# Revit family: GQ Rosenberg 1
name_source: partatom
category: Wyposażenie mechaniczne
revit_build: Autodesk Revit 2017 (Build: 20160225_1515(x64)
units: mm (PartAtom-declared; Revit-internal decimal feet)

## family parameters
Oparty na płaszczyźnie roboczej = Nie
Punkt obliczania pomieszczeń = Nie
Tnij formami wycięć po wczytaniu = Nie
Typ części = Normalny
Współdzielony = Nie
Wymiar okrągłego złącza = Użyj średnicy
Zawsze pionowo = Tak

## types (5) — shared parameters
Częstotliwość = 50 Hz
Data = 09.2018
Klasa szczelnosci silnika (IP) = IP44
Moc = 0 kW
Napięcie = 230 V
Producent = Rosenberg
Prąd = 1 A
Srednica_silnika = 30 mm  [stored 0.0984252 ft]
URL = https://www.rosenberg.pl
Wersja = 1

## per-type parameters (varying)
| type | 200.3BK KS | 250.3BK KS | 300.3BK KS | 350.3DI KS | 400.3DI KS | Ciśnienie | Dlugosc_silnika_przod | Dlugosc_silnika_tyl | Dlugosc_smigla | Grubosc | Grubosc_plyty | Maksymalna dopuszczalna temperatura przetłaczanego medium | Masa | Model | Obroty (1/min) | Promien_wew | Promien_zew | Przepływ poowietrza | Srednica_wew | Srednica_zewnetrzna | Wymiar_obudowy | Wymiar_obudowy/2 |
| 400.3DI KS | Nie | Nie | Nie | Nie | Tak | 65.0 Pa | 41 mm  [stored 0.134514 ft] | 60 mm  [stored 0.19685 ft] | 197 mm  [stored 0.646325 ft] | 88 mm  [stored 0.288714 ft] | 12 mm  [stored 0.0393701 ft] | 45 °C | 7.50 kg | 400.3DI KS | 1430 | 202 mm | 223 mm | 3029.0 m³/h | 403 mm | 445 mm | 540 mm | 270 mm  [stored 0.885827 ft] |
| 250.3BK KS | Nie | Tak | Nie | Nie | Nie | 132.0 Pa | 8 mm  [stored 0.0262467 ft] | 85 mm  [stored 0.278871 ft] | 122 mm | 49 mm  [stored 0.160761 ft] | 6 mm  [stored 0.019685 ft] | 50 °C | 3.50 kg | 250.3BK KS | 2600 | 127 mm | 136 mm | 1152.0 m³/h | 254 mm | 272 mm | 370 mm | 185 mm  [stored 0.606955 ft] |
| 200.3BK KS | Tak | Nie | Nie | Nie | Nie | 132.0 Pa | 15 mm  [stored 0.0492126 ft] | 61 mm  [stored 0.200131 ft] | 95 mm  [stored 0.31168 ft] | 46 mm  [stored 0.150919 ft] | 6 mm  [stored 0.019685 ft] | 50 °C | 1.90 kg | 250.3BK KS | 3375 | 100 mm  [stored 0.328084 ft] | 108 mm | 1152.0 m³/h | 200 mm  [stored 0.656168 ft] | 215 mm | 312 mm | 156 mm  [stored 0.511811 ft] |
| 300.3BK KS | Nie | Nie | Tak | Nie | Nie | 132.0 Pa | 5 mm  [stored 0.0164042 ft] | 60 mm  [stored 0.19685 ft] | 148 mm  [stored 0.485564 ft] | 71 mm  [stored 0.23294 ft] | 11 mm  [stored 0.0360892 ft] | 50 °C | 4.50 kg | 300.3BK KS | 2600 | 153 mm | 165 mm | 1152.0 m³/h | 305 mm  [stored 1.00066 ft] | 330 mm | 430 mm | 215 mm |
| 350.3DI KS | Nie | Nie | Nie | Tak | Nie | 83.0 Pa | 41 mm  [stored 0.134514 ft] | 60 mm  [stored 0.19685 ft] | 174 mm  [stored 0.570866 ft] | 74 mm  [stored 0.242782 ft] | 12 mm  [stored 0.0393701 ft] | 45 °C | 6.40 kg | 350.3DI KS | 1705 | 179 mm  [stored 0.58727 ft] | 193 mm | 2483.0 m³/h | 358 mm | 385 mm | 485 mm | 243 mm |

note: [stored X ft] marks values corroborated as IEEE doubles in the binary element streams (Revit-internal decimal feet)
